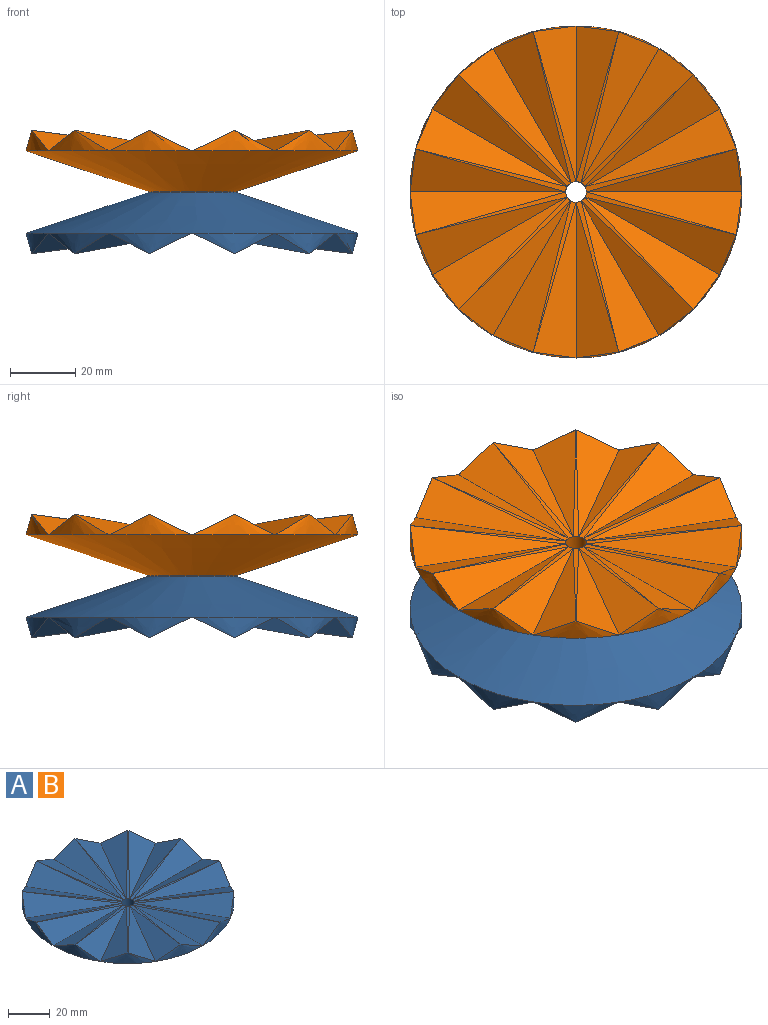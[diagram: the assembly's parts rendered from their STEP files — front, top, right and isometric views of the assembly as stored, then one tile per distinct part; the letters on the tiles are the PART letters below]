
ASSEMBLY  parts=2 mates=1
PART A: 52 faces, bbox 102.5x102.5x20 mm
  f0: plane 23.75x23.75mm, normal (0,0,-1), area 411.4mm2, adj f2,f3
  f1: cone r=12.7mm half-angle=71.6deg, axis (0,0,1), area 7943.9mm2, adj f2,f4,f8,f12,f16,f20,f24,f28
  f2: torus R=11.88mm, axis (0,0,1), area 130.3mm2, adj f0,f1
  f3: cylinder r=3.17mm len=12.7mm, axis (0,0,-1), area 253.4mm2, adj f0,f6,f10,f14,f18,f22,f26,f30
  f4: bspline ~18.59x18.59mm, area 85.1mm2, adj f1,f5,f7
  f5: plane 41.52x34.6mm, normal (0.38,-0.22,0.9), area 347.6mm2, adj f4,f6,f11
  f6: bspline ~34.34x34.33mm, area 26.4mm2, adj f3,f5,f7
  f7: plane 41.8x34.9mm, normal (-0.22,0.38,0.9), area 347.7mm2, adj f4,f6,f49
  f8: bspline ~25.4x6.81mm, area 85.1mm2, adj f1,f9,f11
  f9: plane 47.8x13.32mm, normal (0.43,0,0.9), area 347.6mm2, adj f8,f10,f15
  f10: bspline ~46.32x13.15mm, area 26.4mm2, adj f3,f9,f11
  f11: plane 46.98x24.47mm, normal (-0.38,0.22,0.9), area 347.7mm2, adj f5,f8,f10
  f12: bspline ~25.4x6.81mm, area 83mm2, adj f1,f13,f15
  f13: plane 46.36x23.85mm, normal (0.38,0.22,0.9), area 347.6mm2, adj f12,f14,f19
  f14: bspline ~46.32x13.15mm, area 26.4mm2, adj f3,f13,f15
  f15: plane 48.55x14.08mm, normal (-0.43,0,0.9), area 347.7mm2, adj f9,f12,f14
  f16: bspline ~18.59x18.59mm, area 85.1mm2, adj f1,f17,f19
  f17: plane 41.52x34.6mm, normal (0.22,0.38,0.9), area 347.6mm2, adj f16,f18,f23
  f18: bspline ~34.34x34.33mm, area 26.4mm2, adj f3,f17,f19
  f19: plane 41.8x34.9mm, normal (-0.38,-0.22,0.9), area 347.7mm2, adj f13,f16,f18
  f20: bspline ~25.4x6.81mm, area 85.1mm2, adj f1,f21,f23
  f21: plane 48.13x13.65mm, normal (0,0.43,0.9), area 347.6mm2, adj f20,f22,f27
  f22: bspline ~46.32x13.15mm, area 26.4mm2, adj f3,f21,f23
  f23: plane 46.65x24.14mm, normal (-0.22,-0.38,0.9), area 347.7mm2, adj f17,f20,f22
  f24: bspline ~25.4x6.81mm, area 83mm2, adj f1,f25,f27
  f25: plane 46.36x23.85mm, normal (-0.22,0.38,0.9), area 347.6mm2, adj f24,f26,f31
  f26: bspline ~46.32x13.15mm, area 26.4mm2, adj f3,f25,f27
  f27: plane 48.55x14.08mm, normal (0,-0.43,0.9), area 347.7mm2, adj f21,f24,f26
  f28: bspline ~18.59x18.59mm, area 85.1mm2, adj f1,f29,f31
  f29: plane 41.52x34.6mm, normal (-0.38,0.22,0.9), area 347.6mm2, adj f28,f30,f35
  f30: bspline ~34.34x34.33mm, area 26.4mm2, adj f3,f29,f31
  f31: plane 41.8x34.9mm, normal (0.22,-0.38,0.9), area 347.7mm2, adj f25,f28,f30
  f32: bspline ~25.4x6.81mm, area 85.1mm2, adj f1,f33,f35
  f33: plane 47.8x13.32mm, normal (-0.43,0,0.9), area 347.6mm2, adj f32,f34,f39
  f34: bspline ~46.32x13.15mm, area 26.4mm2, adj f3,f33,f35
  f35: plane 46.98x24.47mm, normal (0.38,-0.22,0.9), area 347.7mm2, adj f29,f32,f34
  f36: bspline ~25.4x6.81mm, area 84.4mm2, adj f1,f37,f39
  f37: plane 46.36x23.85mm, normal (-0.38,-0.22,0.9), area 347.6mm2, adj f36,f38,f43
  f38: bspline ~46.32x13.15mm, area 26.4mm2, adj f3,f37,f39
  f39: plane 48.42x13.94mm, normal (0.43,0,0.9), area 347.7mm2, adj f33,f36,f38
  f40: bspline ~18.59x18.59mm, area 85.1mm2, adj f1,f41,f43
  f41: plane 41.52x34.6mm, normal (-0.22,-0.38,0.9), area 347.6mm2, adj f40,f42,f47
  f42: bspline ~34.34x34.33mm, area 26.4mm2, adj f3,f41,f43
  f43: plane 41.8x34.9mm, normal (0.38,0.22,0.9), area 347.7mm2, adj f37,f40,f42
  f44: bspline ~25.4x6.81mm, area 85.1mm2, adj f1,f45,f47
  f45: plane 47.8x13.32mm, normal (0,-0.43,0.9), area 347.6mm2, adj f44,f46,f51
  f46: bspline ~46.32x13.15mm, area 26.4mm2, adj f3,f45,f47
  f47: plane 46.98x24.47mm, normal (0.22,0.38,0.9), area 347.7mm2, adj f41,f44,f46
  f48: bspline ~25.4x6.81mm, area 84.4mm2, adj f1,f49,f51
  f49: plane 46.36x23.85mm, normal (0.22,-0.38,0.9), area 347.6mm2, adj f7,f48,f50
  f50: bspline ~46.32x13.15mm, area 26.4mm2, adj f3,f49,f51
  f51: plane 48.42x13.94mm, normal (0,0.43,0.9), area 347.7mm2, adj f45,f48,f50
PART B: same geometry as A
PLACE A rot(axis=(0.5,0.87,0),180deg) t=(58.1,-12.7,69.64)mm
PLACE B t=(58.1,-12.7,69.38)mm
MATE revolute B.f1 <-> A.f1  axis (0,0,1) through (58.1,-12.7,69.64)mm
